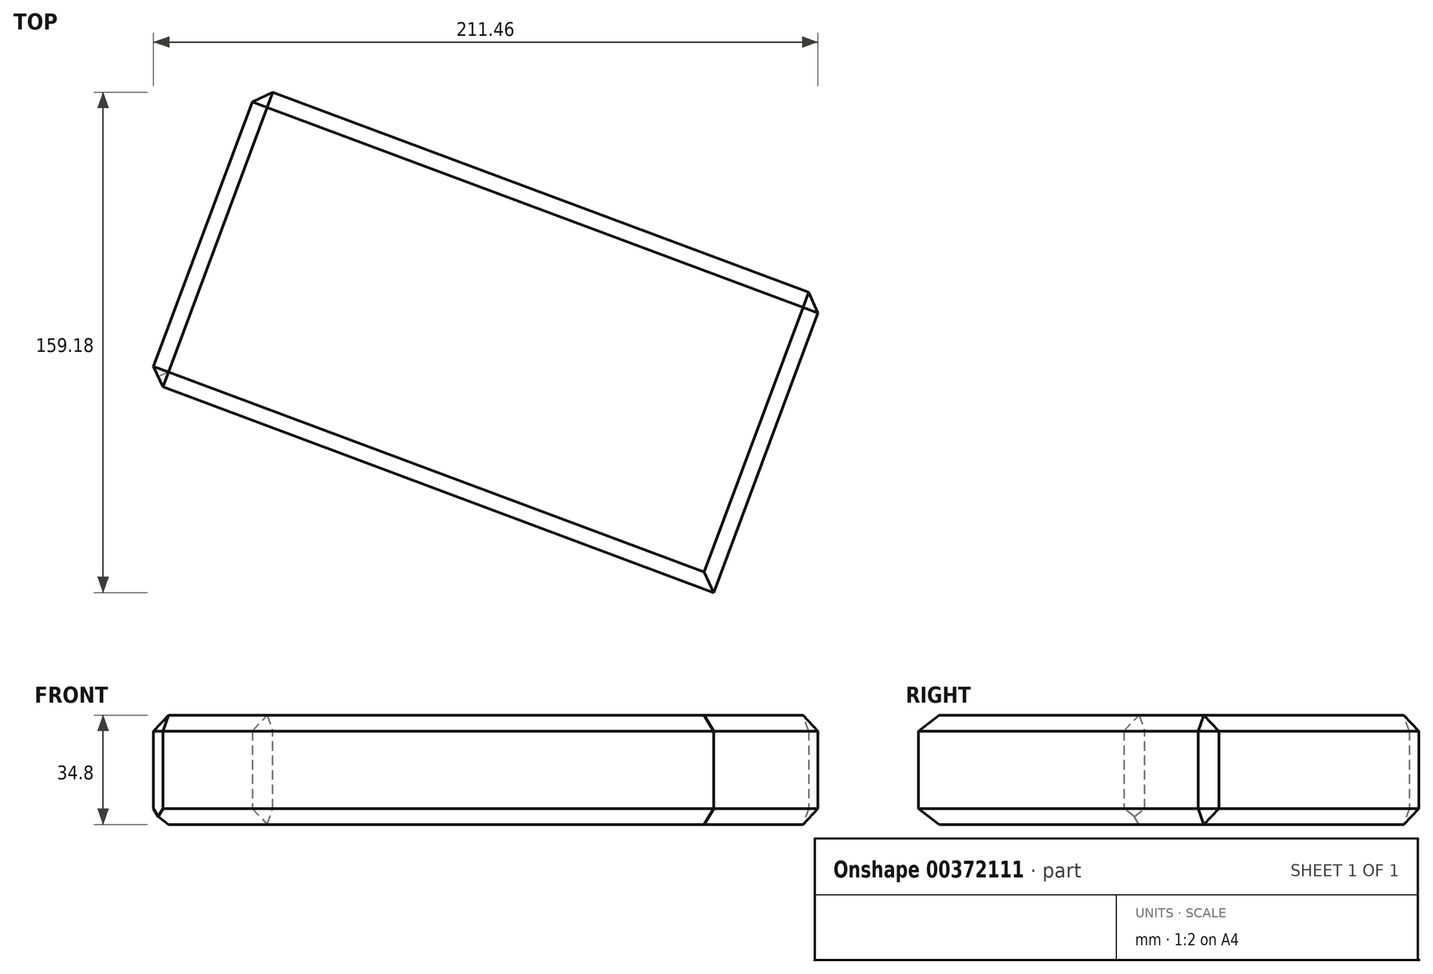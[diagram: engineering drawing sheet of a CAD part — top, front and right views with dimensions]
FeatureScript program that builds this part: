
annotation { "Feature Type Name" : "Feature", "Feature Type Description" : "" }
export const myFeature = defineFeature(function(context is Context, id is Id, definition is map)
    precondition{}
    {
        {
            var Q0;
            Q0=qCreatedBy(makeId("Top.planeOp"),FACE);
            var sketch = newSketch(context, id + "F0", { "sketchPlane" : qUnion([Q0])});
            skLineSegment(sketch, "E0", {"start": v(69.18, -143.25) * mm, "end": v(104.18, -49.48) * mm});
            skLineSegment(sketch, "E1", {"start": v(104.18, -49.48) * mm, "end": v(-75.83, 17.7) * mm});
            skLineSegment(sketch, "E2", {"start": v(-75.83, 17.7) * mm, "end": v(-110.83, -76.06) * mm});
            skLineSegment(sketch, "E3", {"start": v(-110.83, -76.06) * mm, "end": v(69.18, -143.25) * mm});
            skSolve(sketch);
        }
        {
            var Q0;
            Q0 = qSketchRegion(id + "F0", true);
            extrude(context, id + "F1", {"entities" : qUnion([Q0]), "depth" : 34.8 * mm});
        }
        {
            var Q0;
            Q0=makeQuery(id+"F1.opExtrude","CAP_EDGE",EDGE,{"disambiguationData":[OSD([sQuery(id+"F0.wireOp",EDGE,"E1")])],"isStart":false});
            var Q1;
            Q1=makeQuery(id+"F1.opExtrude","SWEPT_EDGE",EDGE,{"disambiguationData":[OSD([sQuery(id+"F0.wireOp",EDGE,"E1"),sQuery(id+"F0.wireOp",EDGE,"E2")])]});
            var Q2;
            Q2=makeQuery(id+"F1.opExtrude","CAP_EDGE",EDGE,{"disambiguationData":[OSD([sQuery(id+"F0.wireOp",EDGE,"E2")])],"isStart":false});
            var Q3;
            Q3=makeQuery(id+"F1.opExtrude","CAP_EDGE",EDGE,{"disambiguationData":[OSD([sQuery(id+"F0.wireOp",EDGE,"E0")])],"isStart":false});
            var Q4;
            Q4=makeQuery(id+"F1.opExtrude","CAP_EDGE",EDGE,{"disambiguationData":[OSD([sQuery(id+"F0.wireOp",EDGE,"E3")])],"isStart":false});
            var Q5;
            Q5=makeQuery(id+"F1.opExtrude","SWEPT_EDGE",EDGE,{"disambiguationData":[OSD([sQuery(id+"F0.wireOp",EDGE,"E0"),sQuery(id+"F0.wireOp",EDGE,"E1")])]});
            var Q6;
            Q6=makeQuery(id+"F1.opExtrude","CAP_EDGE",EDGE,{"disambiguationData":[OSD([sQuery(id+"F0.wireOp",EDGE,"E1")])],"isStart":true});
            var Q7;
            Q7=makeQuery(id+"F1.opExtrude","CAP_EDGE",EDGE,{"disambiguationData":[OSD([sQuery(id+"F0.wireOp",EDGE,"E2")])],"isStart":true});
            var Q8;
            Q8=makeQuery(id+"F1.opExtrude","SWEPT_EDGE",EDGE,{"disambiguationData":[OSD([sQuery(id+"F0.wireOp",EDGE,"E2"),sQuery(id+"F0.wireOp",EDGE,"E3")])]});
            var Q9;
            Q9=makeQuery(id+"F1.opExtrude","CAP_EDGE",EDGE,{"disambiguationData":[OSD([sQuery(id+"F0.wireOp",EDGE,"E0")])],"isStart":true});
            chamfer(context, id + "F2", {"entities" : qUnion([Q0, Q1, Q2, Q3, Q4, Q5, Q6, Q7, Q8, Q9]), "width" : 5.08 * mm, "tangentPropagation" : true});
        }
        {
            var Q0;
            Q0=makeQuery(id+"F1.opExtrude","CAP_EDGE",EDGE,{"disambiguationData":[OSD([sQuery(id+"F0.wireOp",EDGE,"E3")])],"isStart":true});
            chamfer(context, id + "F3", {"entities" : qUnion([Q0]), "width" : 5.08 * mm, "tangentPropagation" : true});
        }
    });
